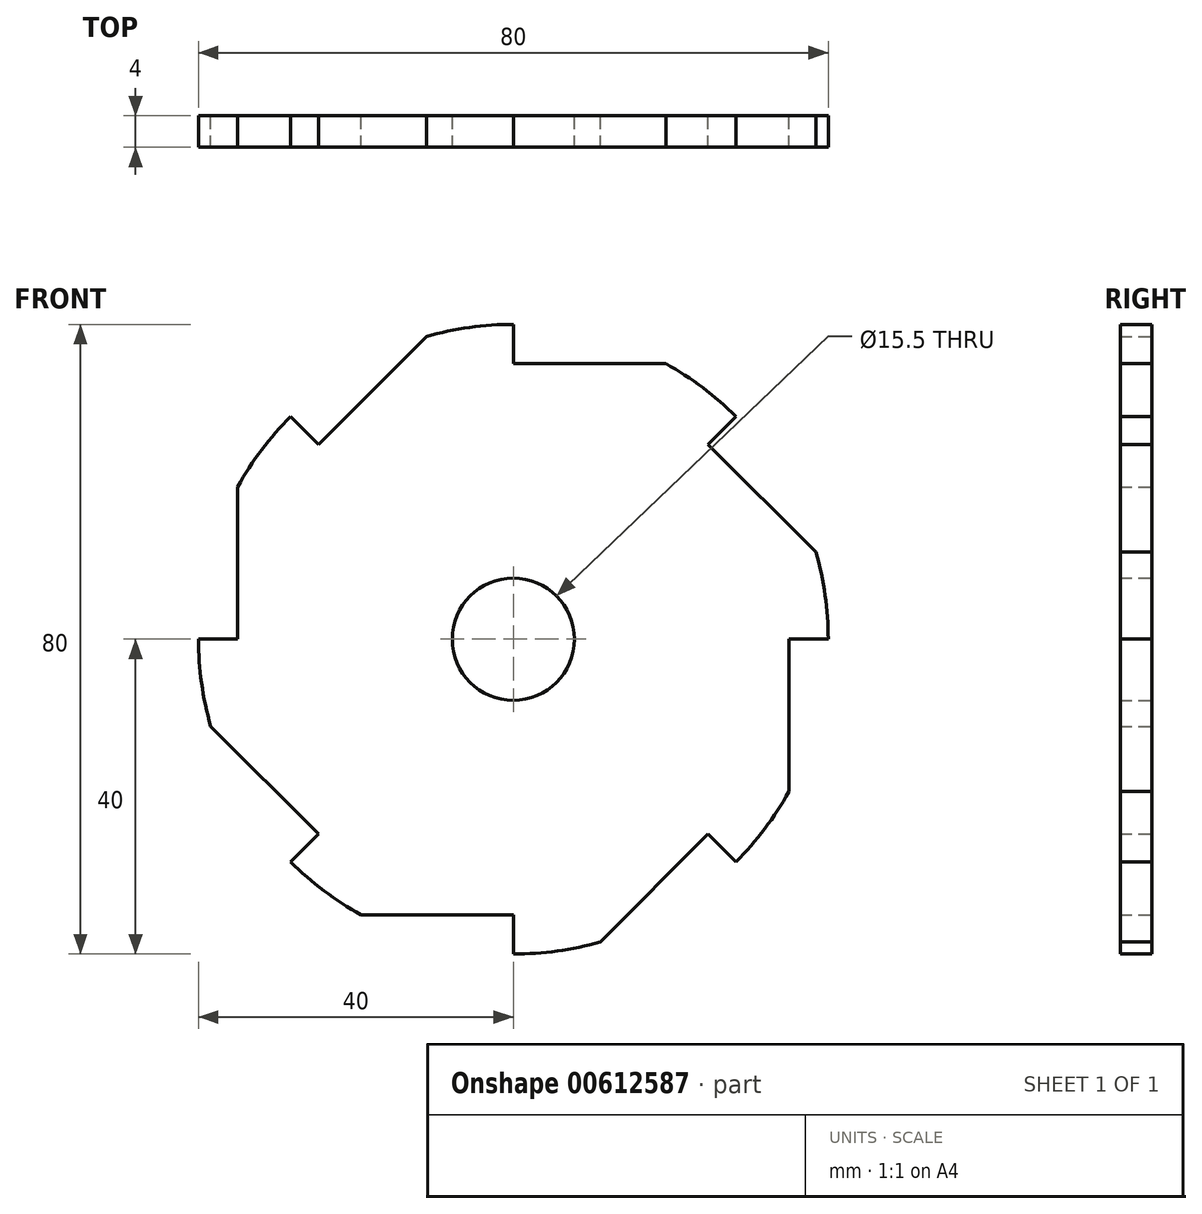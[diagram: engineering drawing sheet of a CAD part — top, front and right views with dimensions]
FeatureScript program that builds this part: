
annotation { "Feature Type Name" : "Feature", "Feature Type Description" : "" }
export const myFeature = defineFeature(function(context is Context, id is Id, definition is map)
    precondition{}
    {
        {
            var Q0;
            Q0=qCreatedBy(makeId("Front.planeOp"),FACE);
            var sketch = newSketch(context, id + "F0", { "sketchPlane" : qUnion([Q0])});
            skCircle(sketch, "E0", {"center": v(0, 0) * mm, "radius": 40 * mm});
            skCircle(sketch, "E1", {"center": v(0, 0) * mm, "radius": 35 * mm});
            skLineSegment(sketch, "E2", {"start": v(0, 40) * mm, "end": v(0, 35) * mm});
            skLineSegment(sketch, "E3", {"start": v(0, 35) * mm, "end": v(19.36, 35) * mm});
            skLineSegment(sketch, "E4.1.0", {"start": v(-28.28, 28.28) * mm, "end": v(-24.75, 24.75) * mm});
            skLineSegment(sketch, "E4.1.1", {"start": v(-24.75, 24.75) * mm, "end": v(-11.06, 38.44) * mm});
            skLineSegment(sketch, "E4.2.0", {"start": v(-40, 0) * mm, "end": v(-35, 0) * mm});
            skLineSegment(sketch, "E4.2.1", {"start": v(-35, 0) * mm, "end": v(-35, 19.36) * mm});
            skLineSegment(sketch, "E4.3.0", {"start": v(-28.28, -28.28) * mm, "end": v(-24.75, -24.75) * mm});
            skLineSegment(sketch, "E4.3.1", {"start": v(-24.75, -24.75) * mm, "end": v(-38.44, -11.06) * mm});
            skLineSegment(sketch, "E4.4.0", {"start": v(0, -40) * mm, "end": v(0, -35) * mm});
            skLineSegment(sketch, "E4.4.1", {"start": v(0, -35) * mm, "end": v(-19.36, -35) * mm});
            skLineSegment(sketch, "E4.5.0", {"start": v(28.28, -28.28) * mm, "end": v(24.75, -24.75) * mm});
            skLineSegment(sketch, "E4.5.1", {"start": v(24.75, -24.75) * mm, "end": v(11.06, -38.44) * mm});
            skLineSegment(sketch, "E4.6.0", {"start": v(40, 0) * mm, "end": v(35, 0) * mm});
            skLineSegment(sketch, "E4.6.1", {"start": v(35, 0) * mm, "end": v(35, -19.36) * mm});
            skLineSegment(sketch, "E4.7.0", {"start": v(28.28, 28.28) * mm, "end": v(24.75, 24.75) * mm});
            skLineSegment(sketch, "E4.7.1", {"start": v(24.75, 24.75) * mm, "end": v(38.44, 11.06) * mm});
            skCircle(sketch, "E5", {"center": v(0, 0) * mm, "radius": 7.75 * mm});
            skSolve(sketch);
        }
        {
            var Q0;
            {var subQ0=sQuery(id+"F0.wireOp",EDGE,"E1");var subQ5=makeQuery(id+"F0.imprint","INTERSECT",VERTEX,{"derivedFrom":[subQ0,sQuery(id+"F0.wireOp",EDGE,"E4.6.0"),sQuery(id+"F0.wireOp",EDGE,"E4.6.1")]});Q0=makeQuery(id+"F0.imprint","IMPRINT",FACE,{"disambiguationData":[TD([[makeQuery(id+"F0.imprint","IMPRINT",EDGE,{"disambiguationData":[TD([[subQ5,-1.0]])],"derivedFrom":subQ0}),1.0]])]});}
            var Q1;
            {var subQ0=sQuery(id+"F0.wireOp",EDGE,"E4.1.0");Q1=makeQuery(id+"F0.imprint","IMPRINT",FACE,{"disambiguationData":[TD([[makeQuery(id+"F0.imprint","IMPRINT",EDGE,{"derivedFrom":subQ0}),-1.0]])]});}
            var Q2;
            {var subQ0=sQuery(id+"F0.wireOp",EDGE,"E2");Q2=makeQuery(id+"F0.imprint","IMPRINT",FACE,{"disambiguationData":[TD([[makeQuery(id+"F0.imprint","IMPRINT",EDGE,{"derivedFrom":subQ0}),-1.0]])]});}
            var Q3;
            {var subQ0=sQuery(id+"F0.wireOp",EDGE,"E3");Q3=makeQuery(id+"F0.imprint","IMPRINT",FACE,{"disambiguationData":[TD([[makeQuery(id+"F0.imprint","IMPRINT",EDGE,{"derivedFrom":subQ0}),-1.0]])]});}
            var Q4;
            {var subQ0=sQuery(id+"F0.wireOp",EDGE,"E4.6.0");Q4=makeQuery(id+"F0.imprint","IMPRINT",FACE,{"disambiguationData":[TD([[makeQuery(id+"F0.imprint","IMPRINT",EDGE,{"derivedFrom":subQ0}),-1.0]])]});}
            var Q5;
            {var subQ0=sQuery(id+"F0.wireOp",EDGE,"E4.5.0");Q5=makeQuery(id+"F0.imprint","IMPRINT",FACE,{"disambiguationData":[TD([[makeQuery(id+"F0.imprint","IMPRINT",EDGE,{"derivedFrom":subQ0}),-1.0]])]});}
            var Q6;
            {var subQ0=sQuery(id+"F0.wireOp",EDGE,"E4.4.0");Q6=makeQuery(id+"F0.imprint","IMPRINT",FACE,{"disambiguationData":[TD([[makeQuery(id+"F0.imprint","IMPRINT",EDGE,{"derivedFrom":subQ0}),-1.0]])]});}
            var Q7;
            {var subQ0=sQuery(id+"F0.wireOp",EDGE,"E4.3.0");Q7=makeQuery(id+"F0.imprint","IMPRINT",FACE,{"disambiguationData":[TD([[makeQuery(id+"F0.imprint","IMPRINT",EDGE,{"derivedFrom":subQ0}),-1.0]])]});}
            var Q8;
            {var subQ0=sQuery(id+"F0.wireOp",EDGE,"E4.2.0");Q8=makeQuery(id+"F0.imprint","IMPRINT",FACE,{"disambiguationData":[TD([[makeQuery(id+"F0.imprint","IMPRINT",EDGE,{"derivedFrom":subQ0}),-1.0]])]});}
            extrude(context, id + "F1", {"entities" : qUnion([Q0, Q1, Q2, Q3, Q4, Q5, Q6, Q7, Q8]), "depth" : 4 * mm, "offsetDistance" : 25.4 * mm});
        }
    });
